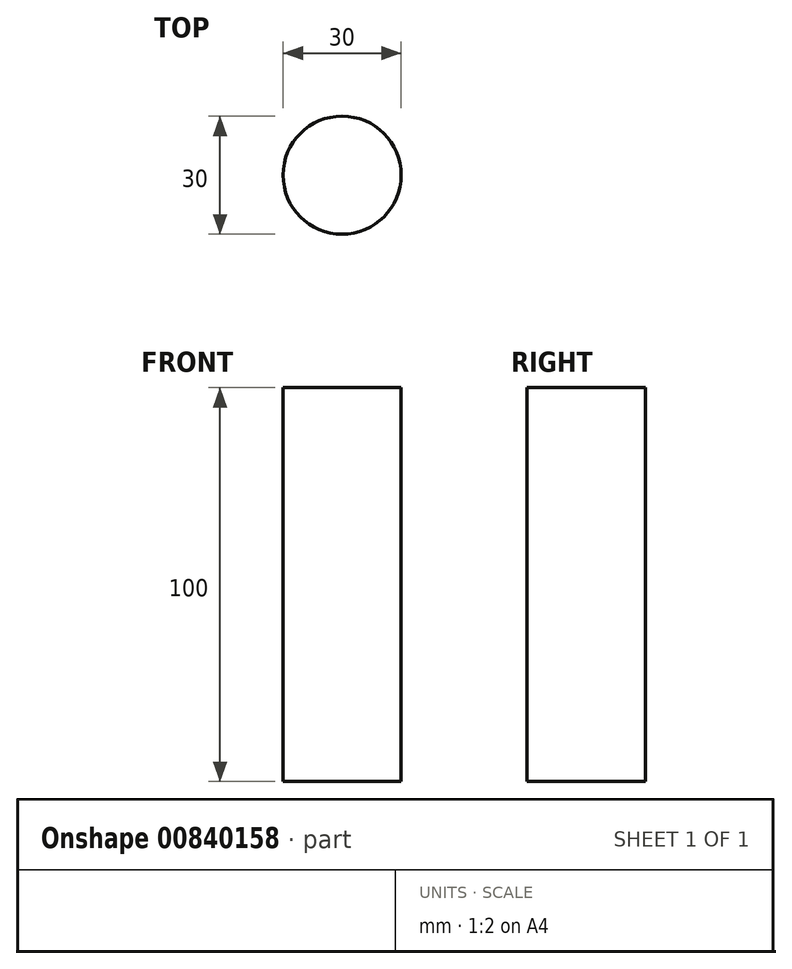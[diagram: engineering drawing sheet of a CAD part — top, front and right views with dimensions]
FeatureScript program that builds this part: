
annotation { "Feature Type Name" : "Feature", "Feature Type Description" : "" }
export const myFeature = defineFeature(function(context is Context, id is Id, definition is map)
    precondition{}
    {
        {
            var Q0;
            Q0=qCreatedBy(makeId("Top.planeOp"),FACE);
            var sketch = newSketch(context, id + "F0", { "sketchPlane" : qUnion([Q0])});
            skCircle(sketch, "E0", {"center": v(0, 0) * mm, "radius": 15 * mm});
            skSolve(sketch);
        }
        {
            var Q0;
            Q0=makeQuery(id+"F0.imprint","IMPRINT",FACE,{"disambiguationData":[TD([[makeQuery(id+"F0.imprint","IMPRINT",EDGE,{"derivedFrom":sQuery(id+"F0.wireOp",EDGE,"E0")}),1.0]])]});
            extrude(context, id + "F1", {"entities" : qUnion([Q0]), "endBound" : BoundingType.SYMMETRIC, "depth" : 100 * mm, "offsetDistance" : 25 * mm});
        }
    });
